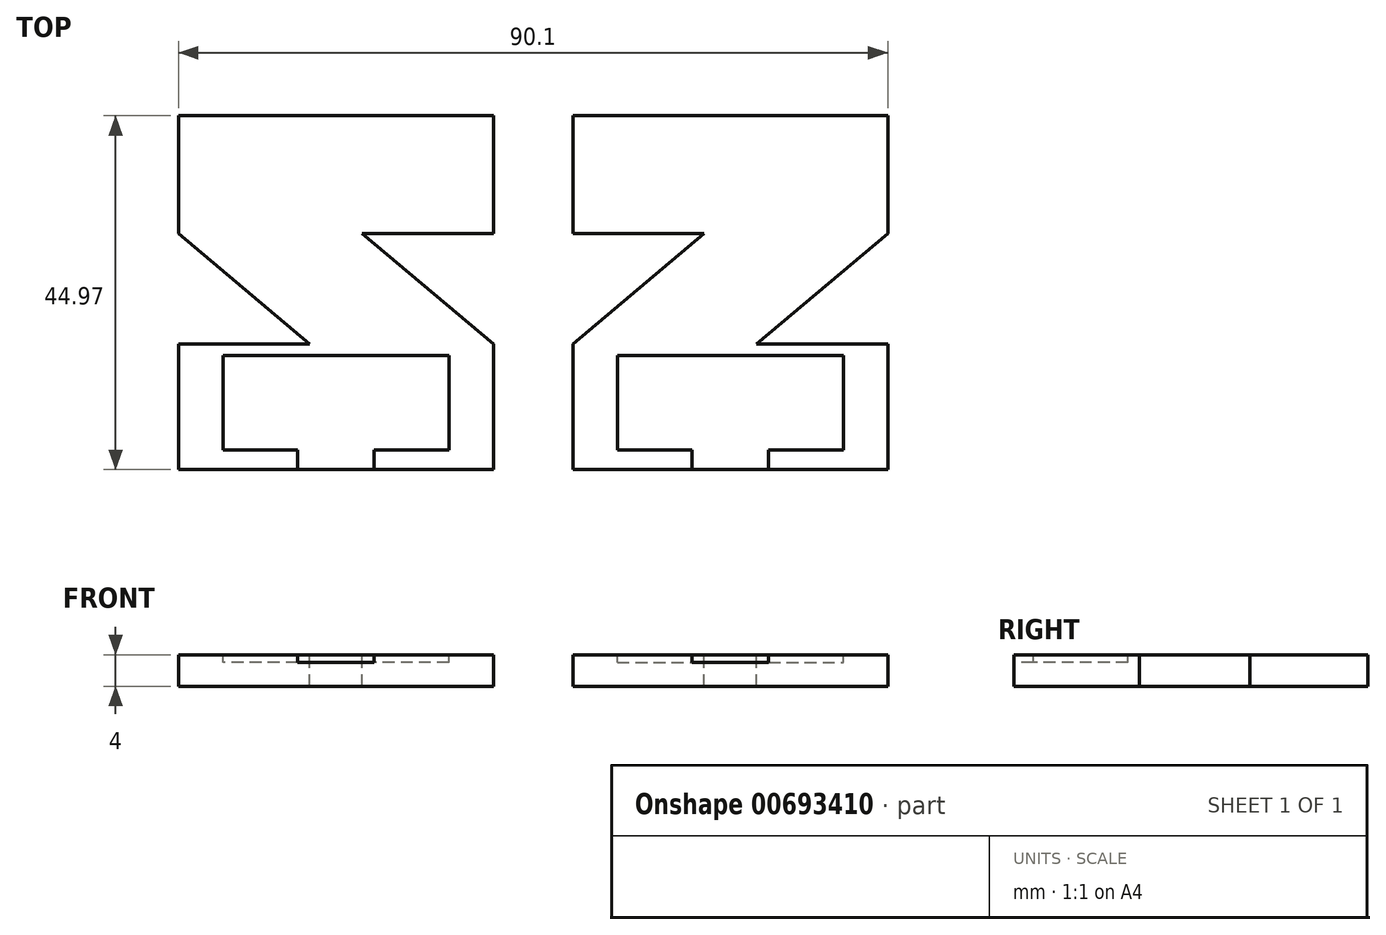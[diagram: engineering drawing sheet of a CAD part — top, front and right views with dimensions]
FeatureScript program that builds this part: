
annotation { "Feature Type Name" : "Feature", "Feature Type Description" : "" }
export const myFeature = defineFeature(function(context is Context, id is Id, definition is map)
    precondition{}
    {
        {
            var Q0;
            Q0=qCreatedBy(makeId("Top.planeOp"),FACE);
            var sketch = newSketch(context, id + "F0", { "sketchPlane" : qUnion([Q0])});
            skLineSegment(sketch, "E0.bottom", {"start": v(0, 0) * mm, "end": v(40, 0) * mm});
            skLineSegment(sketch, "E0.top", {"start": v(0, 15.97) * mm, "end": v(40, 15.97) * mm});
            skLineSegment(sketch, "E0.left", {"start": v(0, 0) * mm, "end": v(0, 15.97) * mm});
            skLineSegment(sketch, "E0.right", {"start": v(40, 0) * mm, "end": v(40, 15.97) * mm});
            skLineSegment(sketch, "E1.bottom", {"start": v(0, 29.97) * mm, "end": v(40, 29.97) * mm});
            skLineSegment(sketch, "E1.top", {"start": v(0, 44.97) * mm, "end": v(40, 44.97) * mm});
            skLineSegment(sketch, "E1.left", {"start": v(0, 29.97) * mm, "end": v(0, 44.97) * mm});
            skLineSegment(sketch, "E1.right", {"start": v(40, 29.97) * mm, "end": v(40, 44.97) * mm});
            skLineSegment(sketch, "E2", {"start": v(40, 29.97) * mm, "end": v(23.33, 15.97) * mm});
            skLineSegment(sketch, "E3", {"start": v(0, 15.97) * mm, "end": v(16.67, 29.97) * mm});
            skLineSegment(sketch, "E4", {"start": v(13.87, 27.62) * mm, "end": v(23.52, 16.13) * mm, "construction": true});
            skLineSegment(sketch, "E5.bottom", {"start": v(5.65, 14.5) * mm, "end": v(34.35, 14.5) * mm});
            skLineSegment(sketch, "E5.top", {"start": v(5.65, 2.5) * mm, "end": v(15.15, 2.5) * mm});
            skLineSegment(sketch, "E5.left", {"start": v(5.65, 14.5) * mm, "end": v(5.65, 2.5) * mm});
            skLineSegment(sketch, "E5.right", {"start": v(34.35, 14.5) * mm, "end": v(34.35, 2.5) * mm});
            skLineSegment(sketch, "E6", {"start": v(0, 10.15) * mm, "end": v(5.65, 10.15) * mm, "construction": true});
            skLineSegment(sketch, "E7", {"start": v(40, 6.95) * mm, "end": v(34.35, 6.95) * mm, "construction": true});
            skLineSegment(sketch, "E8", {"start": v(15.15, 2.5) * mm, "end": v(15.15, 0) * mm});
            skLineSegment(sketch, "E9", {"start": v(15.15, 0) * mm, "end": v(15.01, 0.23) * mm});
            skLineSegment(sketch, "E10", {"start": v(24.85, 2.5) * mm, "end": v(24.85, 0) * mm});
            skLineSegment(sketch, "E11.trimOffspring", {"start": v(24.85, 2.5) * mm, "end": v(34.35, 2.5) * mm});
            skSolve(sketch);
        }
        {
            var Q0;
            Q0 = qSketchRegion(id + "F0", true);
            extrude(context, id + "F1", {"entities" : qUnion([Q0]), "oppositeDirection" : true, "depth" : 4 * mm, "offsetDistance" : 25 * mm});
        }
        {
            var Q0;
            Q0=makeQuery(id+"F0.imprint","IMPRINT",FACE,{"disambiguationData":[TD([[makeQuery(id+"F0.imprint","IMPRINT",EDGE,{"derivedFrom":sQuery(id+"F0.wireOp",EDGE,"E5.bottom")}),-1.0]])]});
            extrude(context, id + "F2", {"entities" : qUnion([Q0]), "operationType" : NewBodyOperationType.REMOVE, "oppositeDirection" : true, "depth" : 1 * mm, "offsetDistance" : 25 * mm});
        }
        {
            var Q0;
            Q0=makeQuery(id+"F1.opExtrude","SWEPT_BODY",BODY,{"disambiguationData":[OSD([sQuery(id+"F0.wireOp",EDGE,"E0.bottom"),sQuery(id+"F0.wireOp",EDGE,"E0.top"),sQuery(id+"F0.wireOp",EDGE,"E0.left"),sQuery(id+"F0.wireOp",EDGE,"E0.right"),sQuery(id+"F0.wireOp",EDGE,"E1.bottom"),sQuery(id+"F0.wireOp",EDGE,"E1.top"),sQuery(id+"F0.wireOp",EDGE,"E1.left"),sQuery(id+"F0.wireOp",EDGE,"E1.right"),sQuery(id+"F0.wireOp",EDGE,"E2"),sQuery(id+"F0.wireOp",EDGE,"E3")])]});
            var Q1;
            Q1=qCreatedBy(makeId("Top.planeOp"),FACE);
            mirror(context, id + "F3", {"entities" : qUnion([Q0]), "mirrorPlane" : qUnion([Q1])});
        }
        {
            var Q0;
            Q0=makeQuery(id+"F3.opPattern","COPY",BODY,{"derivedFrom":makeQuery(id+"F1.opExtrude","SWEPT_BODY",BODY,{"disambiguationData":[OSD([sQuery(id+"F0.wireOp",EDGE,"E0.bottom"),sQuery(id+"F0.wireOp",EDGE,"E0.top"),sQuery(id+"F0.wireOp",EDGE,"E0.left"),sQuery(id+"F0.wireOp",EDGE,"E0.right"),sQuery(id+"F0.wireOp",EDGE,"E1.bottom"),sQuery(id+"F0.wireOp",EDGE,"E1.top"),sQuery(id+"F0.wireOp",EDGE,"E1.left"),sQuery(id+"F0.wireOp",EDGE,"E1.right"),sQuery(id+"F0.wireOp",EDGE,"E2"),sQuery(id+"F0.wireOp",EDGE,"E3")])]}),"instanceName":"1"});
            var Q1;
            Q1=sQuery(id+"F0.wireOp",EDGE,"E0.left");
            transform(context, id + "F4", {"entities" : qUnion([Q0]), "transformType" : TransformType.ROTATION, "transformAxis" : qUnion([Q1]), "angle" : 180 * degree, "makeCopy" : false});
        }
        {
            var Q0;
            Q0=makeQuery(id+"F3.opPattern","COPY",BODY,{"derivedFrom":makeQuery(id+"F1.opExtrude","SWEPT_BODY",BODY,{"disambiguationData":[OSD([sQuery(id+"F0.wireOp",EDGE,"E0.bottom"),sQuery(id+"F0.wireOp",EDGE,"E0.top"),sQuery(id+"F0.wireOp",EDGE,"E0.left"),sQuery(id+"F0.wireOp",EDGE,"E0.right"),sQuery(id+"F0.wireOp",EDGE,"E1.bottom"),sQuery(id+"F0.wireOp",EDGE,"E1.top"),sQuery(id+"F0.wireOp",EDGE,"E1.left"),sQuery(id+"F0.wireOp",EDGE,"E1.right"),sQuery(id+"F0.wireOp",EDGE,"E2"),sQuery(id+"F0.wireOp",EDGE,"E3")])]}),"instanceName":"1"});
            transform(context, id + "F5", {"entities" : qUnion([Q0]), "transformType" : TransformType.TRANSLATION_3D, "dx" : -10.1 * mm, "dy" : 0 * mm, "dz" : 0 * mm, "makeCopy" : false});
        }
    });
